# Revit family: HERZ Drinking Water Mixing Valve With Bottom Mixing Outlet 7766 54
name_source: partatom
category: Rohrzubehör
revit_build: Autodesk Revit 2018 (Build: 20190510_1515(x64)
units: mm (PartAtom-declared; Revit-internal decimal feet)

## family parameters
Arbeitsebenenbasiert = Nein
Beim Laden mit Abzugskörper schneiden = Nein
Bemaßung runder Anschluss = Durchmesser verwenden
Gemeinsam genutzt = Nein
Immer vertikal = Ja
OmniClass-Nummer = 23.65.55.14
OmniClass-Titel = Valves for Liquid Services
Teiletyp = Unterbricht

## types (1)
- HERZ Drinking Water Mixing Valve With Bottom Mixing Outlet 7766 54
    Body = DZR brass CC752S
    Connection thread = flat sealing, G 3/4
    Flow at 3 bar = 0.7 L/s
    H00 = 82 mm  [stored 0.269029 ft]
    H01 = 21 mm  [stored 0.0688976 ft]
    H02 = 9 mm  [stored 0.0295276 ft]
    H03 = 14 mm  [stored 0.0459318 ft]
    H04 = 35 mm  [stored 0.114829 ft]
    H05 = 3 mm  [stored 0.00984252 ft]
    H06 = 25 mm  [stored 0.082021 ft]
    H07 = 62 mm  [stored 0.203412 ft]
    H08 = 8 mm  [stored 0.0262467 ft]
    Hand wheel = ABS
    Hersteller = HERZ Armaturen Ges.m.b.H.
    Internal parts = DZR brass CW626N
    L00 = 40 mm  [stored 0.131234 ft]
    L01 = 12 mm  [stored 0.0393701 ft]
    L02 = 21 mm  [stored 0.0688976 ft]
    LO1 = 59 mm
    Max. dynamic pressure = 0.2 - 6 bar
    Max. hot water inlet temperature = 85 °C
    Max. static pressure = 1000000.0 Pa
    Medium = Water
    Min. cold water inlet temperature range = 5 °C - 25 °C
    Min. flow = 0.1 L/s
    Min. overheat of hot water compared to mixing water = 15 °C
    Mixed water temperature hysteresis = +-2°C
    Mixing temperature (factory setting) = 45 °C
    Nennweite = 20 mm  [stored 0.0656168 ft]
    Note = Pursuant to Article 33 of the REACH Regulation (EC No. 1907/2006), we are obliged to point out that the material lead is listed on the SVHC list and that all brass components manufactured in our products exceed 0.1% (w / w) lead (CAS: 7439-92-1 / EINECS: 231-100-4).
Since lead is a component part of an alloy, actual exposure is not possible and therefore no additional information on safe use is necessary.
    Operation = The thermostatic mixing valve 7766 TMV is used in systems with heated drinking water.
Irrespective of pressure or temperature changes of the cold and hot water to be mixed in the valve, the mixed water is constantly regulated to the preset temperature and flow rate value.
The thermostatic valve works completely independently and without auxiliary energy.
The value of the desired mixing temperature, which is preset once after installation, is kept constant within a control hysteresis.
    Part number = 2776654
    R01 = 8 mm  [stored 0.0262467 ft]
    R02 = 10 mm  [stored 0.0328084 ft]
    R03 = 12 mm  [stored 0.0393701 ft]
    R04 = 24 mm  [stored 0.0787402 ft]
    R05 = 20 mm  [stored 0.0656168 ft]
    R06 = 24 mm  [stored 0.0787402 ft]
    R07 = 4 mm  [stored 0.0131234 ft]
    S01 = 61 mm
    S02 = 38 mm
    SCTWCODE = 04;18;03
    SCTWSEQ = AW;SBT_TYP_AW="104";3
    Safety note = Please note that the applied valve is a safety valve.
It is recommended to replace it in every 5 years.
Local standards and regulations have to be followed
    Sealing = EPDM
    Set value = 35 °C - 50 °C
    Spindle = DZR brass CW626N
    Spring = stainless steel 1.4310
    URL = www.herzvalves.com

note: [stored X ft] marks values corroborated as IEEE doubles in the binary element streams (Revit-internal decimal feet)
